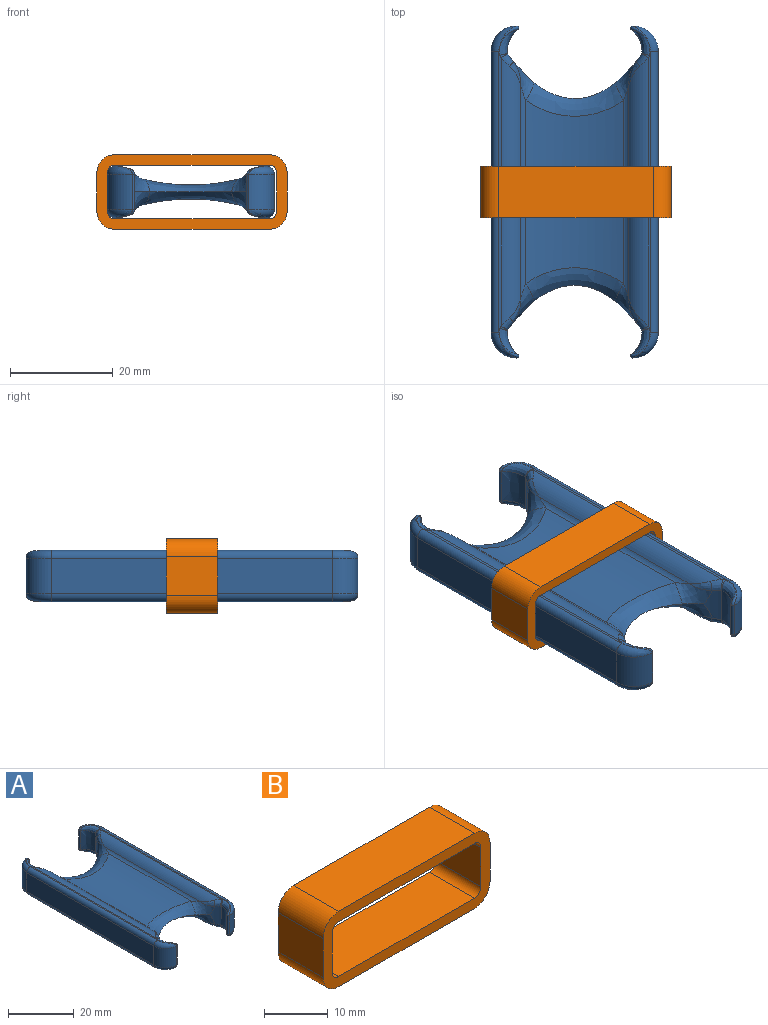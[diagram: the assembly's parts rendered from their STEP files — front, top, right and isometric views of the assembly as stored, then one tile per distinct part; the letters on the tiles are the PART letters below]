
ASSEMBLY  parts=2 mates=1
PART A: 96 faces, bbox 33.4x66.3x10.4 mm
  f0: cylinder r=15.52mm len=7mm, axis (0,0,-1), area 17.7mm2, adj f9,f16,f53,f70,f75,f76,f82
  f1: cylinder r=15.52mm len=7mm, axis (0,0,-1), area 17.7mm2, adj f7,f22,f46,f83,f88,f93,f95
  f2: cylinder r=15.52mm len=7mm, axis (0,0,-1), area 17.7mm2, adj f8,f11,f15,f64,f67,f68,f73
  f3: cylinder r=15.52mm len=7mm, axis (0,0,-1), area 17.7mm2, adj f6,f10,f23,f72,f79,f85,f91
  f4: plane 57.52x0.44mm, normal (0,0,1), area 23.8mm2, adj f10,f11,f43,f44,f45,f47,f51,f71
  f5: plane 57.52x0.44mm, normal (0,0,-1), area 23.8mm2, adj f7,f9,f32,f36,f38,f39,f40,f87
  f6: torus R=17.02mm, axis (0,0,1), area 0.6mm2, adj f3,f27,f29,f79
  f7: torus R=17.02mm, axis (0,0,1), area 0.6mm2, adj f1,f5,f32,f88
  f8: torus R=17.02mm, axis (0,0,1), area 0.6mm2, adj f2,f27,f37,f73
  f9: torus R=17.02mm, axis (0,0,1), area 0.6mm2, adj f0,f5,f40,f82
  f10: torus R=17.02mm, axis (0,0,1), area 0.6mm2, adj f3,f4,f44,f72
  f11: torus R=17.02mm, axis (0,0,1), area 0.6mm2, adj f2,f4,f51,f67
  f12: plane 54.86x7mm, normal (-1,0,0), area 384mm2, adj f13,f25,f31,f45
  f13: cylinder r=4.92mm len=7mm, axis (0,0,-1), area 54.5mm2, adj f12,f14,f33,f47
  f14: cylinder r=0.4mm len=7mm, axis (0,0,-1), area 7.2mm2, adj f13,f15,f35,f49
  f15: extruded ~7x4.57mm, area 36.7mm2, adj f2,f14,f37,f51
  f16: extruded ~7x4.57mm, area 36.7mm2, adj f0,f17,f40,f55
  f17: cylinder r=0.4mm len=7mm, axis (0,0,-1), area 7.2mm2, adj f16,f18,f41,f57
  f18: cylinder r=4.92mm len=7mm, axis (0,0,-1), area 54.5mm2, adj f17,f19,f39,f56
  f19: plane 54.86x7mm, normal (1,0,0), area 384mm2, adj f18,f20,f38,f54
  f20: cylinder r=4.92mm len=7mm, axis (0,0,-1), area 54.5mm2, adj f19,f21,f36,f52
  f21: cylinder r=0.4mm len=7mm, axis (0,0,-1), area 7.2mm2, adj f20,f22,f34,f50
  f22: extruded ~7x4.57mm, area 36.7mm2, adj f1,f21,f32,f48
  f23: extruded ~7x4.57mm, area 36.7mm2, adj f3,f24,f29,f44
  f24: cylinder r=0.4mm len=7mm, axis (0,0,-1), area 7.2mm2, adj f23,f25,f28,f42
  f25: cylinder r=4.92mm len=7mm, axis (0,0,-1), area 54.5mm2, adj f12,f24,f30,f43
  f26: plane 57.52x0.44mm, normal (0,0,1), area 23.8mm2, adj f46,f48,f52,f53,f54,f55,f56,f84
  f27: plane 57.52x0.44mm, normal (0,0,-1), area 23.8mm2, adj f6,f8,f29,f30,f31,f33,f37,f80
  f28: bspline ~4.61x3.59mm, area 1.9mm2, adj f24,f29,f30
  f29: bspline ~6.85x3.95mm, area 9mm2, adj f6,f23,f27,f28
  f30: torus R=3.42mm, axis (0,0,1), area 10.6mm2, adj f25,f27,f28,f31
  f31: cylinder r=1.5mm len=54.86mm, axis (0,-1,0), area 129.3mm2, adj f12,f27,f30,f33
  f32: bspline ~6.85x3.95mm, area 9mm2, adj f5,f7,f22,f34
  f33: torus R=3.42mm, axis (0,0,1), area 10.6mm2, adj f13,f27,f31,f35
  f34: bspline ~4.61x3.59mm, area 1.9mm2, adj f21,f32,f36
  f35: bspline ~4.61x3.59mm, area 1.9mm2, adj f14,f33,f37
  f36: torus R=3.42mm, axis (0,0,1), area 10.6mm2, adj f5,f20,f34,f38
  f37: bspline ~6.85x3.95mm, area 9mm2, adj f8,f15,f27,f35
  f38: cylinder r=1.5mm len=54.86mm, axis (0,1,0), area 129.3mm2, adj f5,f19,f36,f39
  f39: torus R=3.42mm, axis (0,0,1), area 10.6mm2, adj f5,f18,f38,f41
  f40: bspline ~6.85x3.95mm, area 9mm2, adj f5,f9,f16,f41
  f41: bspline ~4.61x3.59mm, area 1.9mm2, adj f17,f39,f40
  f42: bspline ~4.61x3.59mm, area 1.9mm2, adj f24,f43,f44
  f43: torus R=3.42mm, axis (0,0,1), area 10.6mm2, adj f4,f25,f42,f45
  f44: bspline ~6.85x3.95mm, area 9mm2, adj f4,f10,f23,f42
  f45: cylinder r=1.5mm len=54.86mm, axis (0,1,0), area 129.3mm2, adj f4,f12,f43,f47
  f46: torus R=17.02mm, axis (0,0,1), area 0.6mm2, adj f1,f26,f48,f83
  f47: torus R=3.42mm, axis (0,0,1), area 10.6mm2, adj f4,f13,f45,f49
  f48: bspline ~6.85x3.95mm, area 9mm2, adj f22,f26,f46,f50
  f49: bspline ~4.61x3.59mm, area 1.9mm2, adj f14,f47,f51
  f50: bspline ~4.61x3.59mm, area 1.9mm2, adj f21,f48,f52
  f51: bspline ~6.85x3.95mm, area 9mm2, adj f4,f11,f15,f49
  f52: torus R=3.42mm, axis (0,0,1), area 10.6mm2, adj f20,f26,f50,f54
  f53: torus R=17.02mm, axis (0,0,1), area 0.6mm2, adj f0,f26,f55,f76
  f54: cylinder r=1.5mm len=54.86mm, axis (0,-1,0), area 129.3mm2, adj f19,f26,f52,f56
  f55: bspline ~6.85x3.95mm, area 9mm2, adj f16,f26,f53,f57
  f56: torus R=3.42mm, axis (0,0,1), area 10.6mm2, adj f18,f26,f54,f57
  f57: bspline ~4.61x3.59mm, area 1.9mm2, adj f17,f55,f56
  f58: cylinder r=37.94mm len=35.63mm, axis (0,1,0), area 684.3mm2, adj f59,f60,f65,f90
  f59: cylinder r=2mm len=41.25mm, axis (0,1,0), area 47.4mm2, adj f58,f64,f71,f85
  f60: cylinder r=2mm len=41.25mm, axis (0,1,0), area 47.4mm2, adj f58,f70,f84,f93
  f61: cylinder r=37.94mm len=35.63mm, axis (0,1,0), area 684.3mm2, adj f62,f63,f69,f94
  f62: cylinder r=2mm len=41.25mm, axis (0,1,0), area 47.4mm2, adj f61,f68,f80,f91
  f63: cylinder r=2mm len=41.25mm, axis (0,1,0), area 47.4mm2, adj f61,f75,f87,f95
  f64: bspline ~7.96x6.66mm, area 21.4mm2, adj f2,f59,f65,f66,f68
  f65: bspline ~22.45x8.33mm, area 93.1mm2, adj f58,f64,f69,f70
  f66: bspline ~5.56x2.85mm, area 3.5mm2, adj f64,f67,f71
  f67: bspline ~4.58x4.33mm, area 4.5mm2, adj f2,f11,f66,f71
  f68: bspline ~7.96x6.66mm, area 21.5mm2, adj f2,f62,f64,f69,f74
  f69: bspline ~22.45x8.33mm, area 93.1mm2, adj f61,f65,f68,f75
  f70: bspline ~7.96x6.66mm, area 21.5mm2, adj f0,f60,f65,f75,f77
  f71: cylinder r=5mm len=52.28mm, axis (0,1,0), area 205.7mm2, adj f4,f59,f66,f67,f72,f78
  f72: bspline ~3.18x3.17mm, area 4.5mm2, adj f3,f10,f71,f78
  f73: bspline ~4.16x3.94mm, area 4.5mm2, adj f2,f8,f74,f80
  f74: bspline ~5.64x2.96mm, area 3.5mm2, adj f68,f73,f80
  f75: bspline ~7.96x6.66mm, area 21.4mm2, adj f0,f63,f69,f70,f81
  f76: bspline ~4.16x3.94mm, area 4.5mm2, adj f0,f53,f77,f84
  f77: bspline ~5.64x2.96mm, area 3.5mm2, adj f70,f76,f84
  f78: bspline ~5.64x2.96mm, area 3.5mm2, adj f71,f72,f85
  f79: bspline ~3.59x3.56mm, area 4.5mm2, adj f3,f6,f80,f86
  f80: cylinder r=5mm len=52.28mm, axis (0,1,0), area 205.7mm2, adj f27,f62,f73,f74,f79,f86
  f81: bspline ~5.56x2.85mm, area 3.5mm2, adj f75,f82,f87
  f82: bspline ~3.59x3.56mm, area 4.5mm2, adj f0,f9,f81,f87
  f83: bspline ~3.59x3.56mm, area 4.5mm2, adj f1,f46,f84,f89
  f84: cylinder r=5mm len=52.28mm, axis (0,1,0), area 205.7mm2, adj f26,f60,f76,f77,f83,f89
  f85: bspline ~7.96x6.66mm, area 21.5mm2, adj f3,f59,f78,f90,f91
  f86: bspline ~5.56x2.85mm, area 3.5mm2, adj f79,f80,f91
  f87: cylinder r=5mm len=52.28mm, axis (0,1,0), area 205.7mm2, adj f5,f63,f81,f82,f88,f92
  f88: bspline ~3.18x3.17mm, area 4.5mm2, adj f1,f7,f87,f92
  f89: bspline ~5.56x2.85mm, area 3.5mm2, adj f83,f84,f93
  f90: bspline ~22.45x8.33mm, area 93.1mm2, adj f58,f85,f93,f94
  f91: bspline ~7.96x6.66mm, area 21.4mm2, adj f3,f62,f85,f86,f94
  f92: bspline ~5.64x2.96mm, area 3.5mm2, adj f87,f88,f95
  f93: bspline ~7.96x6.66mm, area 21.4mm2, adj f1,f60,f89,f90,f95
  f94: bspline ~22.45x8.33mm, area 93.1mm2, adj f61,f90,f91,f95
  f95: bspline ~7.96x6.66mm, area 21.5mm2, adj f1,f63,f92,f93,f94
PART B: 18 faces, bbox 37.1x10x14.5 mm
  f0: plane 10x7.5mm, normal (1,0,0), area 75mm2, adj f1,f15,f16,f17
  f1: cylinder r=3.5mm len=10mm, axis (0,1,0), area 55mm2, adj f0,f2,f16,f17
  f2: plane 30.08x10mm, normal (0,0,1), area 300.8mm2, adj f1,f3,f16,f17
  f3: cylinder r=3.5mm len=10mm, axis (0,1,0), area 55mm2, adj f2,f4,f16,f17
  f4: plane 10x7.5mm, normal (-1,0,0), area 75mm2, adj f3,f5,f16,f17
  f5: cylinder r=3.5mm len=10mm, axis (0,1,0), area 55mm2, adj f4,f6,f16,f17
  f6: plane 30.08x10mm, normal (0,0,-1), area 300.8mm2, adj f5,f15,f16,f17
  f7: cylinder r=1.5mm len=10mm, axis (0,1,0), area 23.6mm2, adj f8,f14,f16,f17
  f8: plane 10x7.5mm, normal (-1,0,0), area 75mm2, adj f7,f9,f16,f17
  f9: cylinder r=1.5mm len=10mm, axis (0,1,0), area 23.6mm2, adj f8,f10,f16,f17
  f10: plane 30.08x10mm, normal (0,0,1), area 300.8mm2, adj f9,f11,f16,f17
  f11: cylinder r=1.5mm len=10mm, axis (0,1,0), area 23.6mm2, adj f10,f12,f16,f17
  f12: plane 10x7.5mm, normal (1,0,0), area 75mm2, adj f11,f13,f16,f17
  f13: cylinder r=1.5mm len=10mm, axis (0,1,0), area 23.6mm2, adj f12,f14,f16,f17
  f14: plane 30.08x10mm, normal (0,0,-1), area 300.8mm2, adj f7,f13,f16,f17
  f15: cylinder r=3.5mm len=10mm, axis (0,1,0), area 55mm2, adj f0,f6,f16,f17
  f16: plane 37.08x14.5mm, normal (0,-1,0), area 181.7mm2, adj f0,f1,f2,f3,f4,f5,f6,f7
  f17: plane 37.08x14.5mm, normal (0,1,0), area 181.7mm2, adj f0,f1,f2,f3,f4,f5,f6,f7
PLACE A t=(-0.01,0.02,-4.96)mm
PLACE B t=(0.24,5.02,0.04)mm
MATE pin_slot B.f12 <-> A.f12  axis (1,0,0) through (-16.3,0.02,0.04)mm
